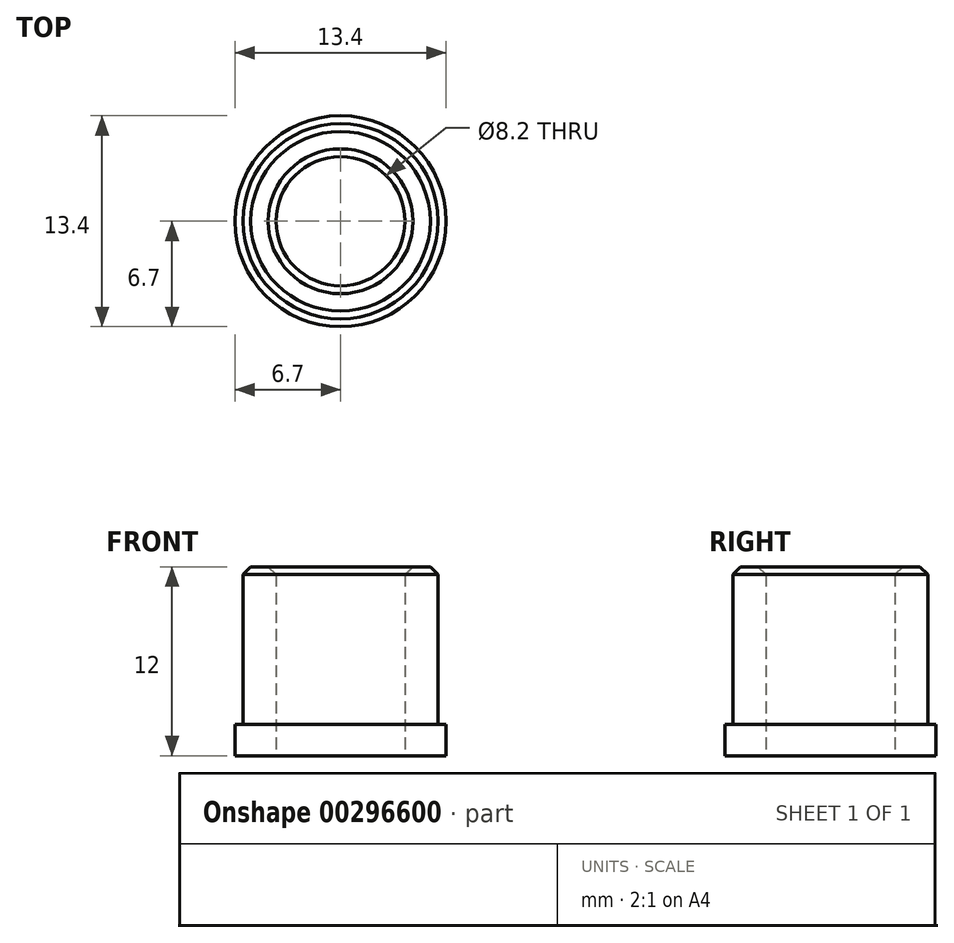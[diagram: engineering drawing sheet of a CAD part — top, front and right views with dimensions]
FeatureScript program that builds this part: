
annotation { "Feature Type Name" : "Feature", "Feature Type Description" : "" }
export const myFeature = defineFeature(function(context is Context, id is Id, definition is map)
    precondition{}
    {
        {
            var Q0;
            Q0=qCreatedBy(makeId("Top.planeOp"),FACE);
            var sketch = newSketch(context, id + "F0", { "sketchPlane" : qUnion([Q0])});
            skCircle(sketch, "E0", {"center": v(0, 0) * mm, "radius": 6.7 * mm});
            skCircle(sketch, "E1", {"center": v(0, 0) * mm, "radius": 4.1 * mm});
            skSolve(sketch);
        }
        {
            var Q0;
            Q0 = qSketchRegion(id + "F0", true);
            extrude(context, id + "F1", {"entities" : qUnion([Q0]), "depth" : 2 * mm});
        }
        {
            var Q0;
            Q0=makeQuery(id+"F1.opExtrude","CAP_FACE",FACE,{"disambiguationData":[OSD([sQuery(id+"F0.wireOp",EDGE,"E0"),sQuery(id+"F0.wireOp",EDGE,"E1")])],"isStart":false});
            var sketch = newSketch(context, id + "F2", { "sketchPlane" : qUnion([Q0])});
            skCircle(sketch, "E2", {"center": v(0, 0) * mm, "radius": 4.1 * mm});
            skCircle(sketch, "E3", {"center": v(0, 0) * mm, "radius": 6.2 * mm});
            skSolve(sketch);
        }
        {
            var Q0;
            Q0 = qSketchRegion(id + "F2", true);
            extrude(context, id + "F3", {"entities" : qUnion([Q0]), "operationType" : NewBodyOperationType.ADD, "depth" : 10 * mm});
        }
        {
            var Q0;
            Q0=makeQuery(id+"F3.opExtrude","CAP_EDGE",EDGE,{"disambiguationData":[OSD([sQuery(id+"F2.wireOp",EDGE,"E2")])],"isStart":false});
            var Q1;
            Q1=makeQuery(id+"F3.opExtrude","CAP_EDGE",EDGE,{"disambiguationData":[OSD([sQuery(id+"F2.wireOp",EDGE,"E3")])],"isStart":false});
            chamfer(context, id + "F4", {"entities" : qUnion([Q0, Q1]), "width" : 0.5 * mm, "tangentPropagation" : true});
        }
    });
